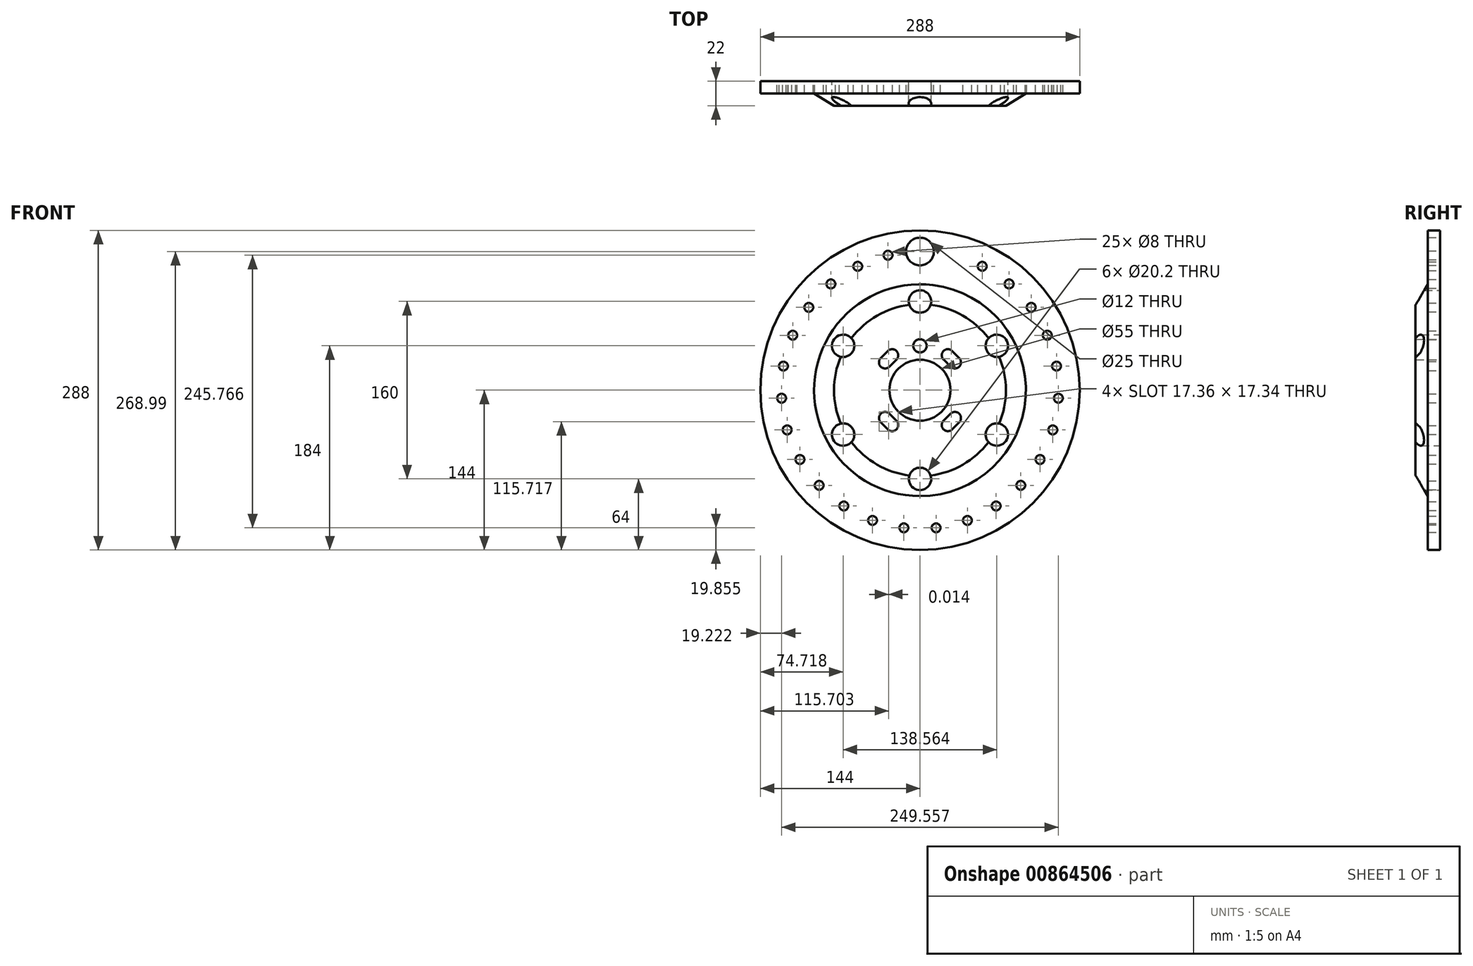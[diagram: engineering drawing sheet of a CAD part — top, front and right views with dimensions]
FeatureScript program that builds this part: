
annotation { "Feature Type Name" : "Feature", "Feature Type Description" : "" }
export const myFeature = defineFeature(function(context is Context, id is Id, definition is map)
    precondition{}
    {
        {
            var Q0;
            Q0=qCreatedBy(makeId("Front.planeOp"),FACE);
            var sketch = newSketch(context, id + "F0", { "sketchPlane" : qUnion([Q0])});
            skCircle(sketch, "E0", {"center": v(0, 0) * mm, "radius": 144 * mm});
            skCircle(sketch, "E1", {"center": v(0, 0) * mm, "radius": 125 * mm, "construction": true});
            skCircle(sketch, "E2.1.0", {"center": v(-28.82, 121.62) * mm, "radius": 4 * mm});
            skCircle(sketch, "E2.2.0", {"center": v(-56.1, 111.7) * mm, "radius": 4 * mm});
            skCircle(sketch, "E2.3.0", {"center": v(-80.34, 95.75) * mm, "radius": 4 * mm});
            skCircle(sketch, "E2.4.0", {"center": v(-100.26, 74.64) * mm, "radius": 4 * mm});
            skCircle(sketch, "E2.5.0", {"center": v(-114.77, 49.5) * mm, "radius": 4 * mm});
            skCircle(sketch, "E2.6.0", {"center": v(-123.1, 21.7) * mm, "radius": 4 * mm});
            skCircle(sketch, "E2.7.0", {"center": v(-124.78, -7.27) * mm, "radius": 4 * mm});
            skCircle(sketch, "E2.8.0", {"center": v(-119.74, -35.85) * mm, "radius": 4 * mm});
            skCircle(sketch, "E2.9.0", {"center": v(-108.24, -62.5) * mm, "radius": 4 * mm});
            skCircle(sketch, "E2.10.0", {"center": v(-90.91, -85.77) * mm, "radius": 4 * mm});
            skCircle(sketch, "E2.11.0", {"center": v(-68.68, -104.43) * mm, "radius": 4 * mm});
            skCircle(sketch, "E2.12.0", {"center": v(-42.75, -117.45) * mm, "radius": 4 * mm});
            skCircle(sketch, "E2.13.0", {"center": v(-14.51, -124.14) * mm, "radius": 4 * mm});
            skCircle(sketch, "E2.14.0", {"center": v(14.51, -124.14) * mm, "radius": 4 * mm});
            skCircle(sketch, "E2.15.0", {"center": v(42.75, -117.45) * mm, "radius": 4 * mm});
            skCircle(sketch, "E2.16.0", {"center": v(68.68, -104.43) * mm, "radius": 4 * mm});
            skCircle(sketch, "E2.17.0", {"center": v(90.91, -85.77) * mm, "radius": 4 * mm});
            skCircle(sketch, "E2.18.0", {"center": v(108.24, -62.5) * mm, "radius": 4 * mm});
            skCircle(sketch, "E2.19.0", {"center": v(119.74, -35.85) * mm, "radius": 4 * mm});
            skCircle(sketch, "E2.20.0", {"center": v(124.78, -7.27) * mm, "radius": 4 * mm});
            skCircle(sketch, "E2.21.0", {"center": v(123.1, 21.7) * mm, "radius": 4 * mm});
            skCircle(sketch, "E2.22.0", {"center": v(114.77, 49.5) * mm, "radius": 4 * mm});
            skCircle(sketch, "E2.23.0", {"center": v(100.26, 74.64) * mm, "radius": 4 * mm});
            skCircle(sketch, "E2.24.0", {"center": v(80.34, 95.75) * mm, "radius": 4 * mm});
            skCircle(sketch, "E2.25.0", {"center": v(56.1, 111.7) * mm, "radius": 4 * mm});
            skCircle(sketch, "E3", {"center": v(0, 125) * mm, "radius": 12.5 * mm});
            skCircle(sketch, "E4", {"center": v(0, 0) * mm, "radius": 27.5 * mm});
            skCircle(sketch, "E5", {"center": v(0, 80) * mm, "radius": 10.1 * mm});
            skCircle(sketch, "E6.1.0", {"center": v(-69.28, 40) * mm, "radius": 10.1 * mm});
            skCircle(sketch, "E6.2.0", {"center": v(-69.28, -40) * mm, "radius": 10.1 * mm});
            skCircle(sketch, "E6.3.0", {"center": v(0, -80) * mm, "radius": 10.1 * mm});
            skCircle(sketch, "E6.4.0", {"center": v(69.28, -40) * mm, "radius": 10.1 * mm});
            skCircle(sketch, "E6.5.0", {"center": v(69.28, 40) * mm, "radius": 10.1 * mm});
            skCircle(sketch, "E7", {"center": v(0, 40) * mm, "radius": 6 * mm});
            skLineSegment(sketch, "E8", {"start": v(0, 40) * mm, "end": v(9, 40) * mm, "construction": true});
            skLineSegment(sketch, "E9", {"start": v(0, 40) * mm, "end": v(-9, 40) * mm, "construction": true});
            skCircle(sketch, "E10.1.0", {"center": v(-25.1, 31.47) * mm, "radius": 5.5 * mm});
            skLineSegment(sketch, "E10.1.1", {"start": v(-35.35, 29) * mm, "end": v(-29, 35.36) * mm});
            skCircle(sketch, "E10.1.2", {"center": v(-31.47, 25.1) * mm, "radius": 5.5 * mm});
            skLineSegment(sketch, "E10.1.3", {"start": v(-28.15, 20.72) * mm, "end": v(-21.23, 27.56) * mm});
            skCircle(sketch, "E10.3.0", {"center": v(-31.47, -25.1) * mm, "radius": 5.5 * mm});
            skLineSegment(sketch, "E10.3.1", {"start": v(-29, -35.35) * mm, "end": v(-35.36, -29) * mm});
            skCircle(sketch, "E10.3.2", {"center": v(-25.1, -31.47) * mm, "radius": 5.5 * mm});
            skLineSegment(sketch, "E10.3.3", {"start": v(-20.72, -28.15) * mm, "end": v(-27.56, -21.23) * mm});
            skCircle(sketch, "E10.5.0", {"center": v(25.1, -31.47) * mm, "radius": 5.5 * mm});
            skLineSegment(sketch, "E10.5.1", {"start": v(35.35, -29) * mm, "end": v(29, -35.36) * mm});
            skCircle(sketch, "E10.5.2", {"center": v(31.47, -25.1) * mm, "radius": 5.5 * mm});
            skLineSegment(sketch, "E10.5.3", {"start": v(28.15, -20.72) * mm, "end": v(21.23, -27.56) * mm});
            skCircle(sketch, "E10.7.0", {"center": v(31.47, 25.1) * mm, "radius": 5.5 * mm});
            skLineSegment(sketch, "E10.7.1", {"start": v(29, 35.35) * mm, "end": v(35.36, 29) * mm});
            skCircle(sketch, "E10.7.2", {"center": v(25.1, 31.47) * mm, "radius": 5.5 * mm});
            skLineSegment(sketch, "E10.7.3", {"start": v(20.72, 28.15) * mm, "end": v(27.56, 21.23) * mm});
            skSolve(sketch);
        }
        {
            var Q0;
            Q0=qCreatedBy(makeId("Right.planeOp"),FACE);
            var sketch = newSketch(context, id + "F1", { "sketchPlane" : qUnion([Q0])});
            skLineSegment(sketch, "E11", {"start": v(0, 0) * mm, "end": v(0, 144) * mm});
            skLineSegment(sketch, "E12", {"start": v(0, 144) * mm, "end": v(-11, 144) * mm});
            skLineSegment(sketch, "E13", {"start": v(-11, 144) * mm, "end": v(-11, 95.5) * mm});
            skLineSegment(sketch, "E14", {"start": v(-11, 95.5) * mm, "end": v(-22, 77.5) * mm});
            skLineSegment(sketch, "E15", {"start": v(-22, 77.5) * mm, "end": v(-22, 0) * mm});
            skLineSegment(sketch, "E16", {"start": v(-22, 0) * mm, "end": v(0, 0) * mm});
            skSolve(sketch);
        }
        {
            var Q0;
            Q0=makeQuery(id+"F1.imprint","IMPRINT",FACE,{"disambiguationData":[TD([[makeQuery(id+"F1.imprint","IMPRINT",EDGE,{"derivedFrom":sQuery(id+"F1.wireOp",EDGE,"E11")}),1.0]])]});
            var Q1;
            Q1=sQuery(id+"F1.wireOp",EDGE,"E16");
            revolve(context, id + "F2", {"surfaceOperationType" : NewSurfaceOperationType.NEW, "entities" : qUnion([Q0]), "axis" : qUnion([Q1]), "revolveType" : RevolveType.FULL});
        }
        {
            var Q0;
            Q0=makeQuery(id+"F0.imprint","IMPRINT",FACE,{"disambiguationData":[TD([[makeQuery(id+"F0.imprint","IMPRINT",EDGE,{"derivedFrom":sQuery(id+"F0.wireOp",EDGE,"E0")}),1.0]])]});
            extrude(context, id + "F3", {"entities" : qUnion([Q0]), "operationType" : NewBodyOperationType.INTERSECT, "depth" : 25 * mm, "offsetDistance" : 25 * mm});
        }
    });
